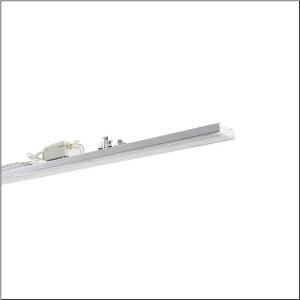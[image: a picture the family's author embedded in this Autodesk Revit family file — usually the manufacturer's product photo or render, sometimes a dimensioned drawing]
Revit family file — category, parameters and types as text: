
# Revit family: licross_11_recessed_mo_51tl19dv4e5g
name_source: partatom
category: Lighting Fixtures
units: mm (PartAtom-declared; Revit-internal decimal feet)

## family parameters
Cut with Voids When Loaded = No
Host = Face
Light Source = No
Part Type = Normal
Room Calculation Point = No
Round Connector Dimension = Use Diameter
Shared = No

## types (1)
- --- (1 x LED, 14720 lm, 84.1 W, 4000K)
    Apparent Load = 84 VA
    CIE Flux Codes = 55 90 98 100 100
    Color Rendering = 80
    Color Temperature = 4000K
    Default Elevation = 1800 mm
    Description = Licross 11 Recessed MO, luminaire insert, of sheet steel, coil coated, white, length: 2.250mm, width: 66mm, height: 67mm, LED rated luminous flux: 14.720lm, light colour: 840, SDCM (Standard Deviation of Colour Matching)MacAdam ≤ 2 SDCM (initial), control gear: DALI 2, with plug, 5-pole, with phase selection, mains connection: 220..240V, AC, 50/60Hz, rated input power: 84W, internal wiring halogen-free, primary light control with lens, of plastic, primary optical cover: cover, of PMMA, light emission: direct distribution, primary light characteristic: double asymmetric, protection rating (complete): IP40, insulation class (complete): insulation class I (protective earthing), certification: CE, ENEC, VDE, UKCA, protection symbol: D if used in an environment without relevant dust loads with corresponding accessories, impact resistance: IK06, permissible ambient temperature for indoor applications: -25..+35°C, corresponds to IFS (International Featured Standards) requirements for safety and quality in the food industry, reducing of maximum allowable ambient temperature of 5°C with ceiling mounting, LABS conformity tested according to VDMA 24364:2018-05, The light source and the operating device comply with the requirements of the Ecodesign Regulation (EU) 2019/2020 and are replaceable in accordance with this regulation, packaging unit: 1 piece
    Height = 58 mm
    Lamp = 1 x LED
    Lamp Light Flux = 14720 lm
    Lamp Power = 84.1 W
    Lamp count = 1
    Length = 2250 mm
    Luminous efficacy = 175 lm/W
    Manufacturer = Siteco
    ModVariant = No
    Model = 51TL19DV4E5G
    Mounting Place = Ceiling
    Mounting Type = Pendant
    Number of Poles = 1
    OnlyDefault = Yes
    Power Factor = 1
    Product Name = Licross 11 Recessed MO
    Product group = luminaire insert | ceiling pendant
    ProductGroupID = 901
    Protection Class = Protection class I
    Protection Degree = IP 40
    RLX_Detail_Level = 1
    RLX_Emergency_Light_Flux = 0 lm
    RLX_Emergency_Type = 0
    RLX_Emergency_Type_DB = No
    RlxData = <blob elided: 29761 chars, md5=0a15488f>
    Socket = socket
    Standby Power = 0 W
    System Light Flux = 14720 lm
    System Power = 84 W
    Type Comments = factory setting: luminous flux: 100 % | dim-lin: 254 | 378 mA
    Type Image = l_1296930.jpg
    URL = http://relux.com
    VarID = @adj_103861
    Voltage = 0 V
    Weight = 0.00 kg
    Width = 66 mm

## geometry (parser evidence)
native form markers: Blend x4, Sweep x9
no freeform markers — native parametric forms only
